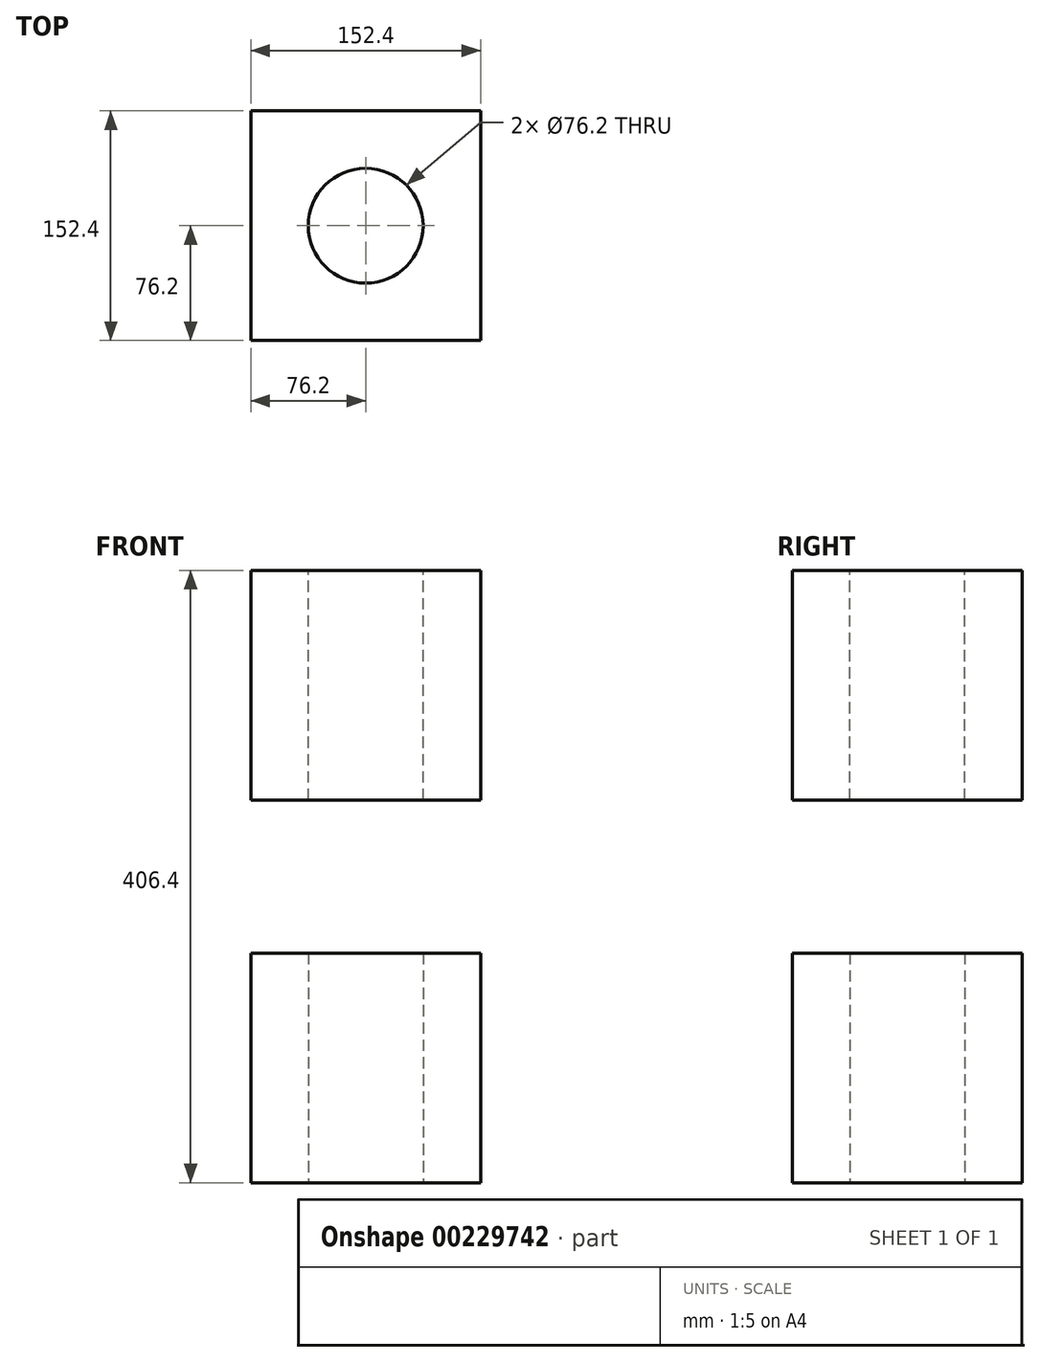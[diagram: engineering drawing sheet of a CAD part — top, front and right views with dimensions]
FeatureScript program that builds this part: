
annotation { "Feature Type Name" : "Feature", "Feature Type Description" : "" }
export const myFeature = defineFeature(function(context is Context, id is Id, definition is map)
    precondition{}
    {
        {
            var Q0;
            Q0=qCreatedBy(makeId("Top.planeOp"),FACE);
            var sketch = newSketch(context, id + "F0", { "sketchPlane" : qUnion([Q0])});
            skLineSegment(sketch, "E0.bottom", {"start": v(-76.2, 76.2) * mm, "end": v(76.2, 76.2) * mm});
            skLineSegment(sketch, "E0.top", {"start": v(-76.2, -76.2) * mm, "end": v(76.2, -76.2) * mm});
            skLineSegment(sketch, "E0.left", {"start": v(-76.2, 76.2) * mm, "end": v(-76.2, -76.2) * mm});
            skLineSegment(sketch, "E0.right", {"start": v(76.2, 76.2) * mm, "end": v(76.2, -76.2) * mm});
            skPoint(sketch, "E0.middle", {"position": v(0, 0) * mm});
            skSolve(sketch);
        }
        {
            var Q0;
            Q0=makeQuery(id+"F0.imprint","IMPRINT",FACE,{"disambiguationData":[TD([[makeQuery(id+"F0.imprint","IMPRINT",EDGE,{"derivedFrom":sQuery(id+"F0.wireOp",EDGE,"E0.bottom")}),-1.0]])]});
            extrude(context, id + "F1", {"entities" : qUnion([Q0]), "depth" : 152.4 * mm});
        }
        {
            var Q0;
            Q0=makeQuery(id+"F1.opExtrude","CAP_FACE",FACE,{"disambiguationData":[OSD([sQuery(id+"F0.wireOp",EDGE,"E0.bottom"),sQuery(id+"F0.wireOp",EDGE,"E0.top"),sQuery(id+"F0.wireOp",EDGE,"E0.left"),sQuery(id+"F0.wireOp",EDGE,"E0.right")])],"isStart":false});
            var sketch = newSketch(context, id + "F2", { "sketchPlane" : qUnion([Q0])});
            skLineSegment(sketch, "E1", {"start": v(0, 76.2) * mm, "end": v(0, -76.2) * mm, "construction": true});
            skLineSegment(sketch, "E2", {"start": v(-76.2, 0) * mm, "end": v(76.2, 0) * mm, "construction": true});
            skCircle(sketch, "E3", {"center": v(0, 0) * mm, "radius": 38.1 * mm});
            skSolve(sketch);
        }
        {
            var Q0;
            Q0=makeQuery(id+"F2.imprint","IMPRINT",FACE,{"disambiguationData":[TD([[makeQuery(id+"F2.imprint","IMPRINT",EDGE,{"derivedFrom":sQuery(id+"F2.wireOp",EDGE,"E3")}),1.0]])]});
            var Q1;
            Q1=makeQuery(id+"F1.opExtrude","CAP_FACE",FACE,{"disambiguationData":[OSD([sQuery(id+"F0.wireOp",EDGE,"E0.bottom"),sQuery(id+"F0.wireOp",EDGE,"E0.top"),sQuery(id+"F0.wireOp",EDGE,"E0.left"),sQuery(id+"F0.wireOp",EDGE,"E0.right")])],"isStart":true});
            extrude(context, id + "F3", {"entities" : qUnion([Q0]), "operationType" : NewBodyOperationType.REMOVE, "endBound" : BoundingType.UP_TO_SURFACE, "oppositeDirection" : true, "endBoundEntityFace" : qUnion([Q1]), "depth" : 25.4 * mm});
        }
        {
            var Q0;
            Q0=qCreatedBy(makeId("Top.planeOp"),FACE);
            cPlane(context, id + "F4", {"entities" : qUnion([Q0]), "cplaneType" : CPlaneType.OFFSET, "offset" : 50.8 * mm, "oppositeDirection" : true, "width" : 152.4 * mm, "height" : 152.4 * mm});
        }
        {
            var Q0;
            Q0=makeQuery(id+"F1.opExtrude","SWEPT_BODY",BODY,{"disambiguationData":[OSD([sQuery(id+"F0.wireOp",EDGE,"E0.bottom"),sQuery(id+"F0.wireOp",EDGE,"E0.top"),sQuery(id+"F0.wireOp",EDGE,"E0.left"),sQuery(id+"F0.wireOp",EDGE,"E0.right")])]});
            var Q1;
            Q1=qCreatedBy(id+"F4.planeOp",FACE);
            mirror(context, id + "F5", {"entities" : qUnion([Q0]), "mirrorPlane" : qUnion([Q1])});
        }
    });
